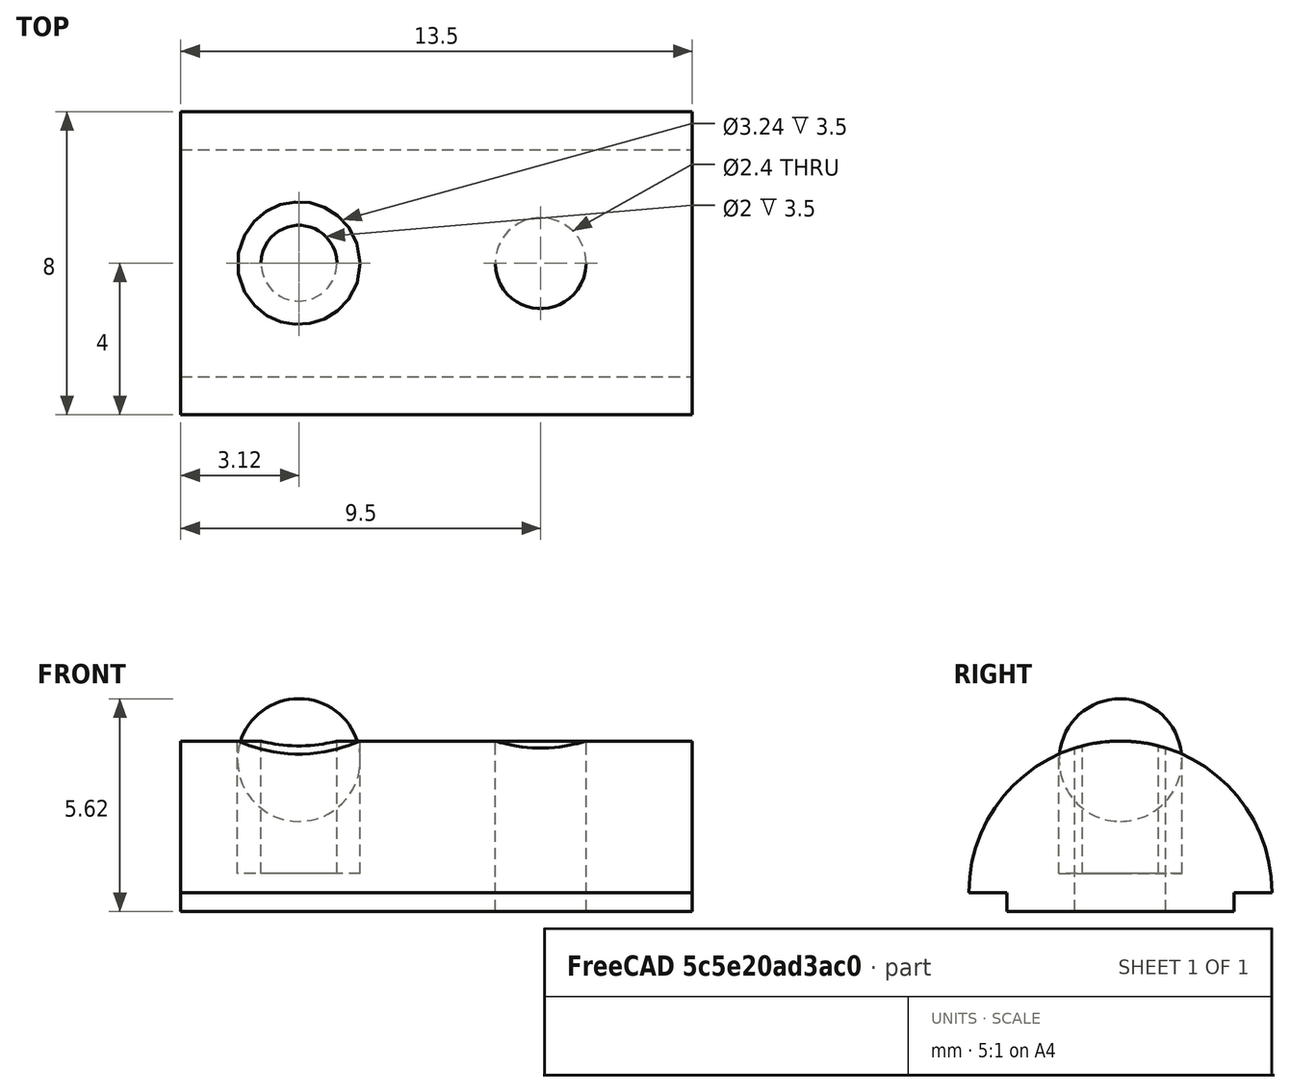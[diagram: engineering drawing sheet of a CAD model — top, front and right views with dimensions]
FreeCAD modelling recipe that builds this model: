
FCSTD DOCUMENT  (FreeCAD 0.17R13050 (Git))
Label: T-slot_2020_round_roll-in_nut_M3
License: All rights reserved
LicenseURL: http://en.wikipedia.org/wiki/All_rights_reserved
objects: Part::Cylinder×3, Part::Cut×2, Part::Sphere×1, Part::Box×1, Part::MultiFuse×1, Part::Feature×1, App::Part×1
note: 9 computed .brp shape members not serialized (recipe doc carries the construction recipe); baked Part::Feature solids carry a one-line shape summary decoded from their .brp

FEATURE [Part::Cylinder] Cylinder002
  Angle = 360
  AttacherType = Attacher::AttachEngine3D
  Height = 4.5
  Placement = pos=(9.5,3,0) rot=(0,0,1;0rad)
  Radius = 1.2
FEATURE [Part::Sphere] Sphere
  Angle1 = -90
  Angle2 = 90
  Angle3 = 360
  AttacherType = Attacher::AttachEngine3D
  Placement = pos=(3.12,3,4) rot=(0,1,0;1.5708rad)
  Radius = 1.62
FEATURE [Part::Cylinder] Cylinder001
  Angle = 360
  AttacherType = Attacher::AttachEngine3D
  Height = 3.5
  Placement = pos=(3.12,3,1) rot=(0,0,1;0rad)
  Radius = 1
FEATURE [Part::Cylinder] Cylinder
  Angle = 180
  AttacherType = Attacher::AttachEngine3D
  Height = 13.5
  Placement = pos=(0,3,0.5) rot=(0.57735,0.57735,0.57735;2.0944rad)
  Radius = 4
FEATURE [Part::Box] Box  label="Cube"
  AttacherType = Attacher::AttachEngine3D
  Height = 0.5
  Length = 13.5
  Width = 6
FEATURE [Part::MultiFuse] Fusion
  Shapes = -> [Cylinder,Box]
FEATURE [Part::Cut] Cut  label="src"
  Base = -> Fusion
  Tool = -> Cylinder001
FEATURE [Part::Feature] Cut001
  shape: bbox 13.5 x 8 x 4.5 mm, 10 faces (baked)
FEATURE [Part::Cut] Cut002
  Base = -> Cut001
  Tool = -> Cylinder002
FEATURE [App::Part] Part  label="T-slot_2020_round_roll-in_nut_M3"
  Group = -> [Sphere,Cylinder001,Cylinder,Fusion,Box,Cut,Cut001,Cylinder002,Cut002]
  License = CC BY 3.0
  LicenseURL = http://creativecommons.org/licenses/by/3.0/
  Origin = -> Origin
